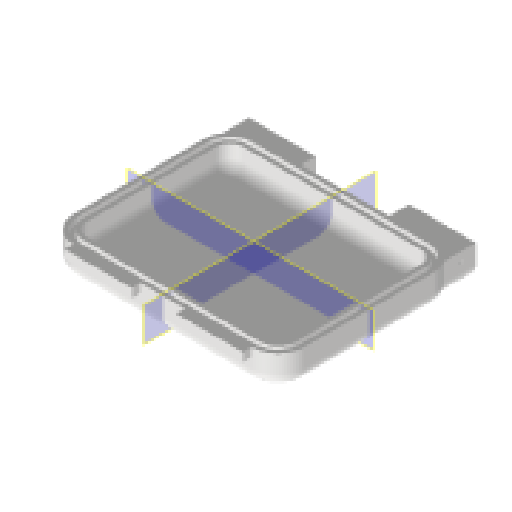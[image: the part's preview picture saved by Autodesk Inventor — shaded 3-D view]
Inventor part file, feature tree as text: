
AUTODESK INVENTOR PART (.ipt)
format: ipt  version: 2024.1 (Build 281209000, 209)  size: 2,323,456 bytes
history: native  units: mm
features: extrude x5, sketch x5, other x3, projected_geometry x3, plane x2, fillet x1, reference x1
ambient origin geometry x8: Origin, YZ Plane, XZ Plane, XY Plane, X Axis, Y Axis, Z Axis, Center Point
bodies: Volumenkörper1 (feature_tree)
feature tree (20):
  extrude  "Extrusion1"  Depth=233.0mm
  extrude  "Extrusion2"  Depth=15.0mm
  fillet  "Rundung1"  Radius=30.0mm
  extrude  "Extrusion3"  Depth=15.0mm
  extrude  "Extrusion4"  Depth=5.0mm
  plane  "Arbeitsebene1"
  plane  "Arbeitsebene2"
  extrude  "Extrusion5"  Depth=5.0mm
  sketch  "Skizze1"  dims[d10=233.0mm d11=178.0mm]
  other  "Bild1"
  sketch  "Skizze2"  dims[d13=15.0mm d14=15.0mm d15=30.0mm d16=0.0mm]
  projected_geometry  "Projizierte Kontur1"
  sketch  "Skizze3"  dims[d17=6.0mm d18=0.0mm d19=15.0mm]
  projected_geometry  "Projizierte Kontur2"
  sketch  "Skizze4"  dims[d20=5.0mm d21=5.0mm]
  projected_geometry  "Projizierte Kontur3"
  sketch  "Skizze5"  dims[d22=6.0mm d23=0.0mm d24=5.0mm d25=17.0mm d26=76.0mm d27=5.0mm d28=76.0mm d30=76.0mm d31=10.0mm d32=76.0mm d33=10.0mm d34=0.0mm d35=0.0mm d36=0.0mm]
  reference  "Referenz1"
  other  "Assembly_Planktoscope_Uc2version_wormdrive_V3.iam"
  other  "00_OutdoorCase_Type2000_base:1"
